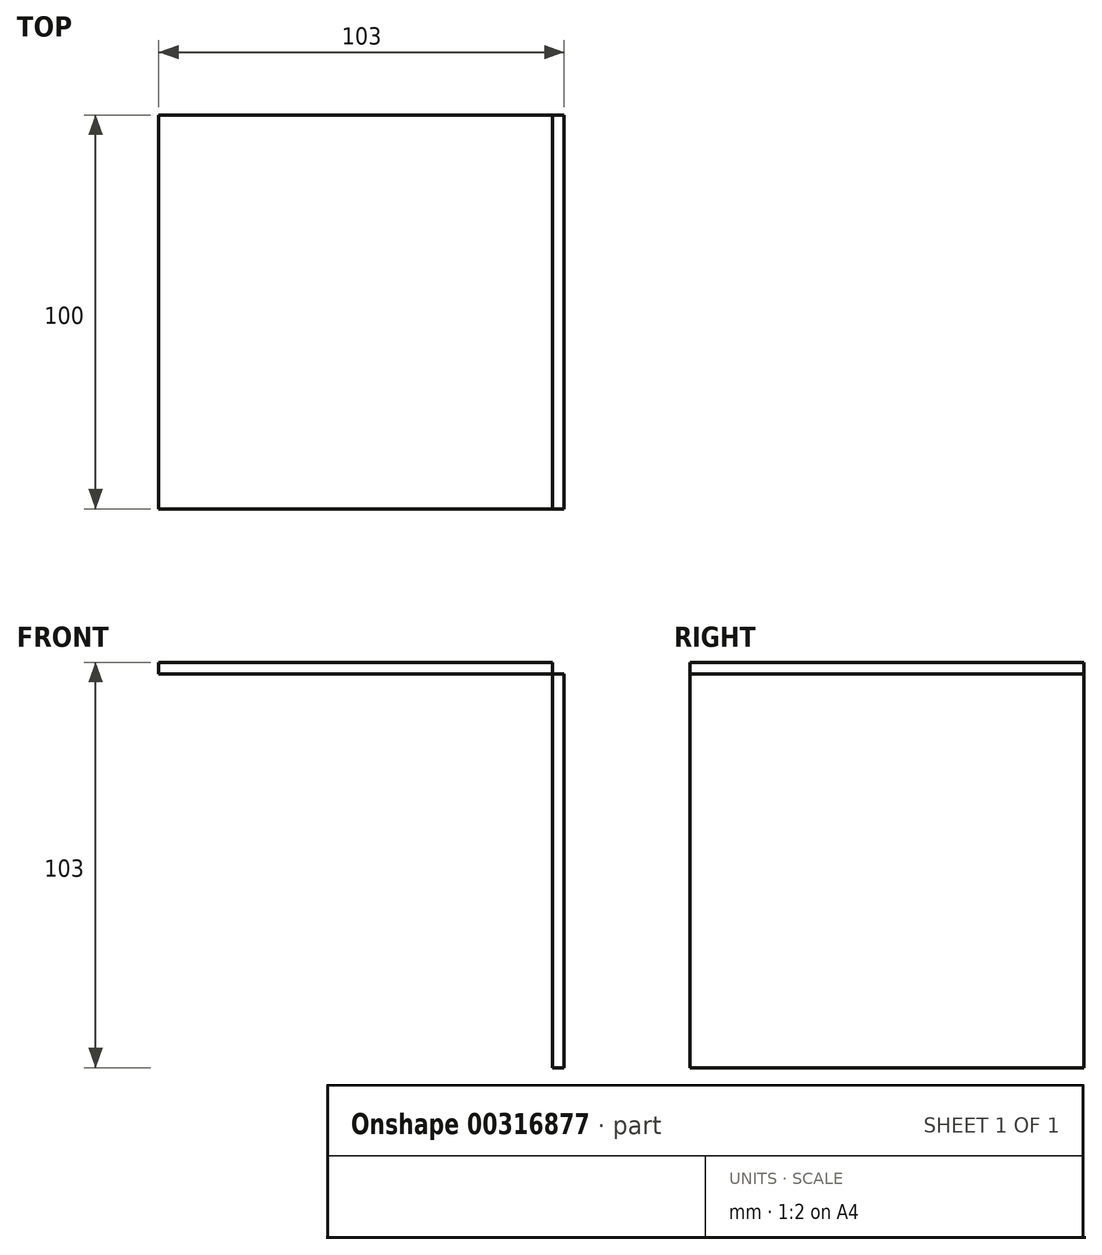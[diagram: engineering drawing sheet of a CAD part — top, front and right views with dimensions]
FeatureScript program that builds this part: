
annotation { "Feature Type Name" : "Feature", "Feature Type Description" : "" }
export const myFeature = defineFeature(function(context is Context, id is Id, definition is map)
    precondition{}
    {
        {
            assignVariable(context, id + "F0", {"name" : "mtrl", "anyValue" : 3 * mm});
        }
        {
            var Q0;
            Q0=qCreatedBy(makeId("Right.planeOp"),FACE);
            cPlane(context, id + "F1", {"entities" : qUnion([Q0]), "cplaneType" : CPlaneType.OFFSET, "offset" : 50 * mm, "width" : 150 * mm, "height" : 150 * mm});
        }
        {
            var Q0;
            Q0=qCreatedBy(id+"F1.planeOp",FACE);
            var sketch = newSketch(context, id + "F2", { "sketchPlane" : qUnion([Q0])});
            skLineSegment(sketch, "E0.bottom", {"start": v(-50, 0) * mm, "end": v(50, 0) * mm});
            skLineSegment(sketch, "E0.top", {"start": v(-50, -100) * mm, "end": v(50, -100) * mm});
            skLineSegment(sketch, "E0.left", {"start": v(-50, 0) * mm, "end": v(-50, -100) * mm});
            skLineSegment(sketch, "E0.right", {"start": v(50, 0) * mm, "end": v(50, -100) * mm});
            skPoint(sketch, "E0.middle", {"position": v(0, -50) * mm});
            skSolve(sketch);
        }
        {
            var Q0;
            Q0 = qSketchRegion(id + "F2", true);
            extrude(context, id + "F3", {"entities" : qUnion([Q0]), "depth" : getVariable(context, 'mtrl')});
        }
        {
            var Q0;
            Q0=qCreatedBy(makeId("Top.planeOp"),FACE);
            var sketch = newSketch(context, id + "F4", { "sketchPlane" : qUnion([Q0])});
            skLineSegment(sketch, "E1.bottom", {"start": v(50, -50) * mm, "end": v(-50, -50) * mm});
            skLineSegment(sketch, "E1.top", {"start": v(50, 50) * mm, "end": v(-50, 50) * mm});
            skLineSegment(sketch, "E1.left", {"start": v(50, -50) * mm, "end": v(50, 50) * mm});
            skLineSegment(sketch, "E1.right", {"start": v(-50, -50) * mm, "end": v(-50, 50) * mm});
            skPoint(sketch, "E1.middle", {"position": v(0, 0) * mm});
            skSolve(sketch);
        }
        {
            var Q0;
            Q0=makeQuery(id+"F4.imprint","IMPRINT",FACE,{"disambiguationData":[TD([[makeQuery(id+"F4.imprint","IMPRINT",EDGE,{"derivedFrom":sQuery(id+"F4.wireOp",EDGE,"E1.bottom")}),-1.0]])]});
            extrude(context, id + "F5", {"entities" : qUnion([Q0]), "depth" : getVariable(context, 'mtrl')});
        }
    });
